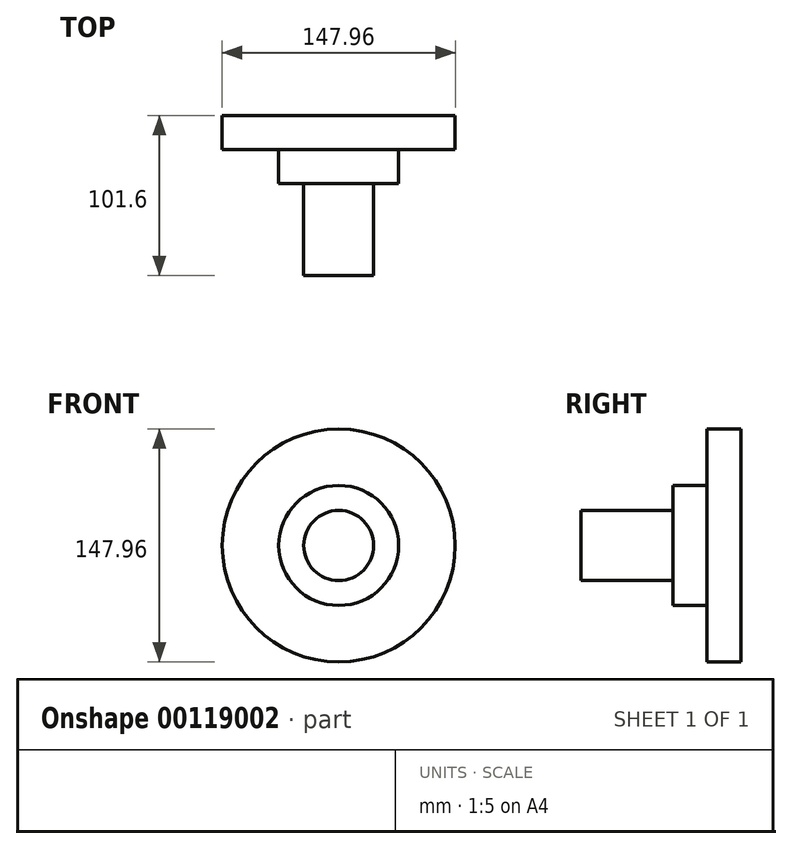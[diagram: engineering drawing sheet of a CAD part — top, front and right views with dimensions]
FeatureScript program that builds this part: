
annotation { "Feature Type Name" : "Feature", "Feature Type Description" : "" }
export const myFeature = defineFeature(function(context is Context, id is Id, definition is map)
    precondition{}
    {
        {
            var Q0;
            Q0=qCreatedBy(makeId("Front.planeOp"),FACE);
            var sketch = newSketch(context, id + "F0", { "sketchPlane" : qUnion([Q0])});
            skCircle(sketch, "E0", {"center": v(0, 0) * mm, "radius": 73.98 * mm});
            skSolve(sketch);
        }
        {
            var Q0;
            Q0=makeQuery(id+"F0.imprint","IMPRINT",FACE,{"disambiguationData":[TD([[makeQuery(id+"F0.imprint","IMPRINT",EDGE,{"derivedFrom":sQuery(id+"F0.wireOp",EDGE,"E0")}),1.0]])]});
            extrude(context, id + "F1", {"entities" : qUnion([Q0]), "depth" : 21.59 * mm});
        }
        {
            var Q0;
            Q0=makeQuery(id+"F1.opExtrude","CAP_FACE",FACE,{"disambiguationData":[OSD([sQuery(id+"F0.wireOp",EDGE,"E0")])],"isStart":false});
            var sketch = newSketch(context, id + "F2", { "sketchPlane" : qUnion([Q0])});
            skCircle(sketch, "E1", {"center": v(0, 0) * mm, "radius": 38.1 * mm});
            skSolve(sketch);
        }
        {
            var Q0;
            Q0=makeQuery(id+"F2.imprint","IMPRINT",FACE,{"disambiguationData":[TD([[makeQuery(id+"F2.imprint","IMPRINT",EDGE,{"derivedFrom":sQuery(id+"F2.wireOp",EDGE,"E1")}),1.0]])]});
            extrude(context, id + "F3", {"entities" : qUnion([Q0]), "operationType" : NewBodyOperationType.ADD, "depth" : 21.59 * mm});
        }
        {
            var Q0;
            Q0=makeQuery(id+"F3.opExtrude","CAP_FACE",FACE,{"disambiguationData":[OSD([sQuery(id+"F2.wireOp",EDGE,"E1")])],"isStart":false});
            var sketch = newSketch(context, id + "F4", { "sketchPlane" : qUnion([Q0])});
            skCircle(sketch, "E2", {"center": v(0, 0) * mm, "radius": 22.23 * mm});
            skSolve(sketch);
        }
        {
            var Q0;
            Q0=makeQuery(id+"F4.imprint","IMPRINT",FACE,{"disambiguationData":[TD([[makeQuery(id+"F4.imprint","IMPRINT",EDGE,{"derivedFrom":sQuery(id+"F4.wireOp",EDGE,"E2")}),1.0]])]});
            extrude(context, id + "F5", {"entities" : qUnion([Q0]), "operationType" : NewBodyOperationType.ADD, "depth" : 58.42 * mm});
        }
    });
